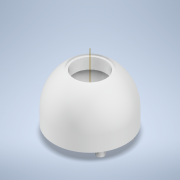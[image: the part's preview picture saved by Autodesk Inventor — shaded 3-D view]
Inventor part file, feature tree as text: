
AUTODESK INVENTOR PART (.ipt)
format: ipt  version: 2021 (Build 250183000, 183)  size: 598,528 bytes
history: native  units: in
note: dims shown in document units (in); Inventor stores cm internally (conversion verified against a paired STEP export)
features: sketch x7, extrude x6, fillet x2, other x1, revolve x1, pattern_circular x1, mirror x1, chamfer x1
ambient origin geometry x8: Origin, YZ Plane, XZ Plane, XY Plane, X Axis, Y Axis, Z Axis, Center Point
bodies: Solid1 (feature_tree)
feature tree (20):
  extrude  "Extrusion1"  Depth=1.0236in
  other  "Work Axis1"
  revolve  "Revolution1"  [1 undecoded]
  extrude  "Extrusion2"  Depth=1.0079in
  extrude  "Extrusion3"  TaperAngle=90.0deg  [1 undecoded]
  extrude  "Extrusion4"  Depth=0.8976in
  extrude  "Extrusion5"  Depth=1.0236in TaperAngle=0.0deg
  pattern_circular  "Circular Pattern1"  [2 undecoded]
  mirror  "Mirror1"
  fillet  "Fillet2"  Radius=0.8268in
  extrude  "Extrusion7"  Depth=0.1969in TaperAngle=0.0deg
  chamfer  "Chamfer2"  Distance=1.9685in Angle=240.0deg
  fillet  "Fillet3"  Radius=0.5039in
  sketch  "Sketch1"  dims[d0=2.0472in d1=1.0236in]
  sketch  "Sketch2"  dims[d2=1.0236in d3=1.0236in]
  sketch  "Sketch3"  dims[d4=1.378in d5=0.0in d6=1.0079in]
  sketch  "Sketch4"  dims[d7=90.0deg d8=90.0deg]
  sketch  "Sketch5"  dims[d9=0.0394in d10=0.0in d11=0.8976in]
  sketch  "Sketch8"  dims[d12=0.0in d13=0.0in d14=1.0236in d15=0.0in]
  sketch  "Sketch10"  dims[d16=1.2913in d21=0.2126in d22=0.8268in d23=0.1969in d24=0.0in d25=1.9685in d26=240.0deg d33=0.5039in d34=0.0394in d35=0.7079in d36=0.3937in d37=0.3539in d38=0.2362in d39=0.3937in d40=0.0in d41=0.3937in d42=0.2283in d43=45.0deg d44=0.1969in d45=0.0197in d46=0.0344in d47=0.0197in d48=0.0344in]
note: 4 required parameter values undecoded (feature->parameter linkage not recoverable at this tier; creation-order binding heuristic only, values carry confidence <= 0.55)